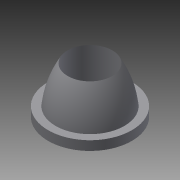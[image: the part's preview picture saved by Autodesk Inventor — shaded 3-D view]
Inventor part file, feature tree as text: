
AUTODESK INVENTOR PART (.ipt)
format: ipt  version: 2013 SP2 (Build 170200200, 200)  size: 99,840 bytes
history: native  units: mm
features: revolve x1
ambient origin geometry x8: Origin, YZ Plane, XZ Plane, XY Plane, X Axis, Y Axis, Z Axis, Center Point
bodies: Solid1 (feature_tree)
feature tree (1):
  revolve  "Revolution1"  [1 undecoded]
note: 1 required parameter value undecoded (feature->parameter linkage not recoverable at this tier; creation-order binding heuristic only, values carry confidence <= 0.55)
